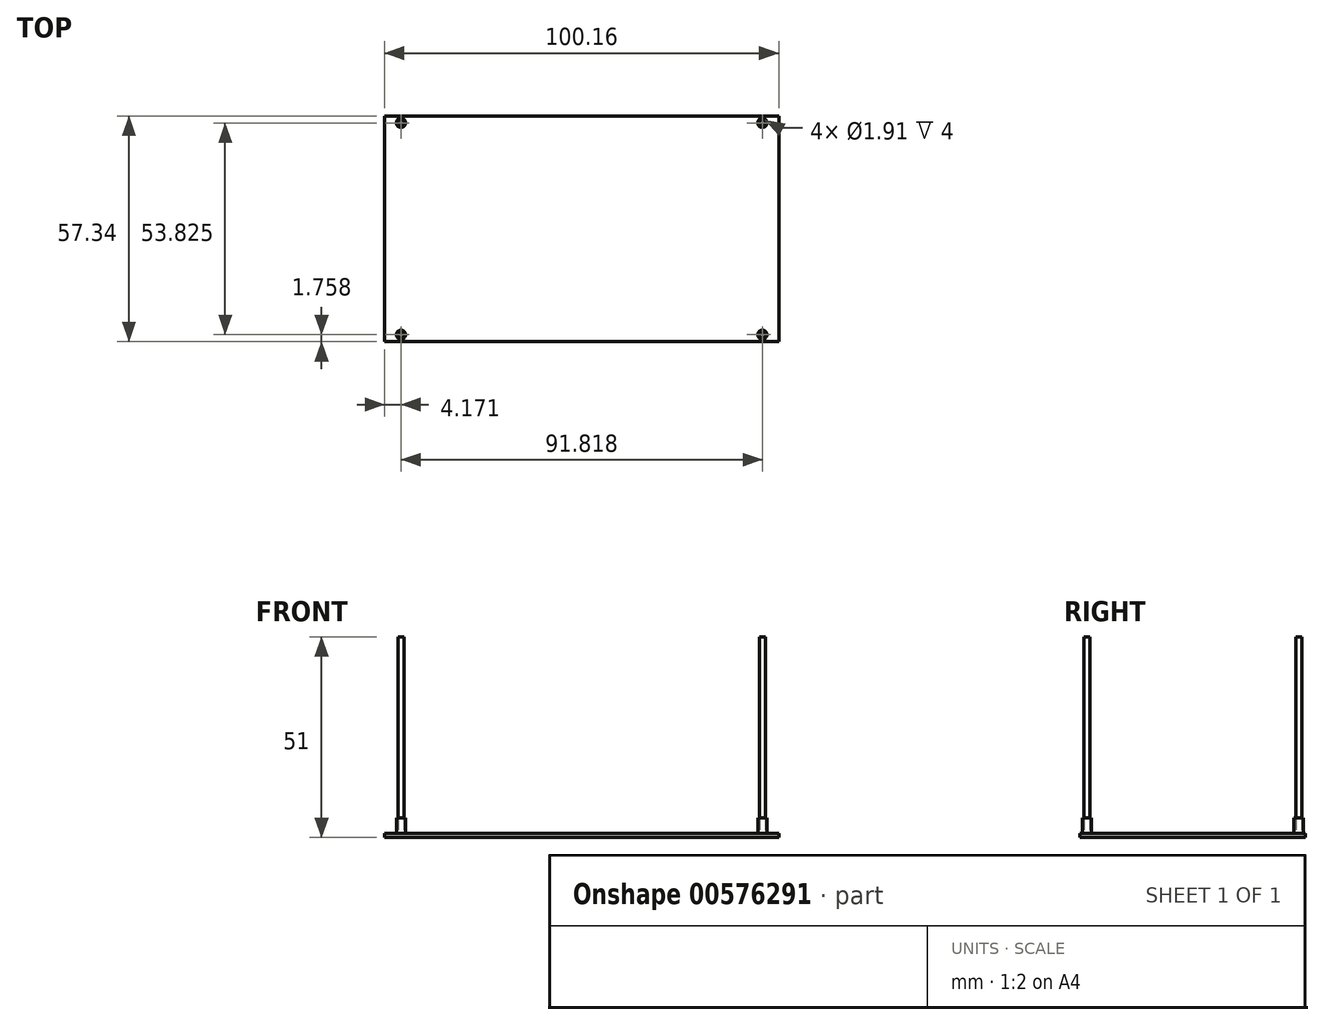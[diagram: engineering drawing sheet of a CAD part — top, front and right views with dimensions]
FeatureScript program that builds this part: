
annotation { "Feature Type Name" : "Feature", "Feature Type Description" : "" }
export const myFeature = defineFeature(function(context is Context, id is Id, definition is map)
    precondition{}
    {
        {
            var Q0;
            Q0=qCreatedBy(makeId("Top.planeOp"),FACE);
            var sketch = newSketch(context, id + "F0", { "sketchPlane" : qUnion([Q0])});
            skLineSegment(sketch, "E0.bottom", {"start": v(50.08, 28.67) * mm, "end": v(-50.08, 28.67) * mm});
            skLineSegment(sketch, "E0.top", {"start": v(50.08, -28.67) * mm, "end": v(-50.08, -28.67) * mm});
            skLineSegment(sketch, "E0.left", {"start": v(50.08, 28.67) * mm, "end": v(50.08, -28.67) * mm});
            skLineSegment(sketch, "E0.right", {"start": v(-50.08, 28.67) * mm, "end": v(-50.08, -28.67) * mm});
            skPoint(sketch, "E0.middle", {"position": v(0, 0) * mm});
            skSolve(sketch);
        }
        {
            var Q0;
            Q0 = qSketchRegion(id + "F0", true);
            extrude(context, id + "F1", {"entities" : qUnion([Q0]), "depth" : 1 * mm, "offsetDistance" : 25 * mm});
        }
        {
            var Q0;
            Q0=qCreatedBy(makeId("Top.planeOp"),FACE);
            var sketch = newSketch(context, id + "F2", { "sketchPlane" : qUnion([Q0])});
            skLineSegment(sketch, "E1", {"start": v(-50.08, 28.67) * mm, "end": v(-48.08, 28.67) * mm});
            skLineSegment(sketch, "E2", {"start": v(-48.08, 28.67) * mm, "end": v(-48.08, 26.67) * mm});
            skLineSegment(sketch, "E3", {"start": v(-48.08, 26.67) * mm, "end": v(-50.08, 26.67) * mm});
            skLineSegment(sketch, "E4", {"start": v(-50.08, 26.67) * mm, "end": v(-50.08, 28.67) * mm});
            skSolve(sketch);
        }
        {
            var Q0;
            Q0=makeQuery(id+"F1.opExtrude","CAP_FACE",FACE,{"disambiguationData":[OSD([sQuery(id+"F0.wireOp",EDGE,"E0.bottom"),sQuery(id+"F0.wireOp",EDGE,"E0.top"),sQuery(id+"F0.wireOp",EDGE,"E0.left"),sQuery(id+"F0.wireOp",EDGE,"E0.right")])],"isStart":false});
            var sketch = newSketch(context, id + "F3", { "sketchPlane" : qUnion([Q0])});
            skLineSegment(sketch, "E5", {"start": v(0, 0) * mm, "end": v(-64.87, 0) * mm, "construction": true});
            skPoint(sketch, "E5.endSnap0", {"position": v(-50.08, 0) * mm});
            skLineSegment(sketch, "E6", {"start": v(0, 0) * mm, "end": v(0, 40.05) * mm, "construction": true});
            skSolve(sketch);
        }
        {
            var Q0;
            Q0=makeQuery(id+"F3.imprint","IMPRINT",FACE,{"disambiguationData":[TD([[makeQuery(id+"F3.imprint","IMPRINT",EDGE,{"derivedFrom":makeQuery(id+"F1.opExtrude","CAP_EDGE",EDGE,{"disambiguationData":[OSD([sQuery(id+"F0.wireOp",EDGE,"E0.bottom")])],"isStart":false})}),1.0]])]});
            var sketch = newSketch(context, id + "F4", { "sketchPlane" : qUnion([Q0])});
            skCircle(sketch, "E7", {"center": v(-45.9, 26.92) * mm, "radius": 0.75 * mm});
            skSolve(sketch);
        }
        {
            var Q0;
            Q0 = qSketchRegion(id + "F4", true);
            var Q1;
            Q1=sQuery(id+"F4.wireOp",EDGE,"E7");
            extrude(context, id + "F5", {"entities" : qUnion([Q0]), "surfaceEntities" : qUnion([Q1]), "depth" : 50 * mm, "offsetDistance" : 25 * mm});
        }
        {
            var Q0;
            Q0=qCreatedBy(makeId("Top.planeOp"),FACE);
            var sketch = newSketch(context, id + "F6", { "sketchPlane" : qUnion([Q0])});
            skCircle(sketch, "E8", {"center": v(-45.9, 26.91) * mm, "radius": 0.95 * mm});
            skCircle(sketch, "E9", {"center": v(-45.9, 26.91) * mm, "radius": 1.16 * mm});
            skSolve(sketch);
        }
        {
            var Q0;
            Q0 = qSketchRegion(id + "F6", true);
            extrude(context, id + "F7", {"entities" : qUnion([Q0]), "depth" : 5 * mm, "offsetDistance" : 25 * mm});
        }
        {
            var Q0;
            Q0=makeQuery(id+"FUAeHRYxmnNsWtS_1.opExtrude","SWEPT_BODY",BODY,{"disambiguationData":[OSD([sQuery(id+"F2.wireOp",EDGE,"E1"),sQuery(id+"F2.wireOp",EDGE,"E2"),sQuery(id+"F2.wireOp",EDGE,"E3"),sQuery(id+"F2.wireOp",EDGE,"E4")])]});
            var Q1;
            Q1=makeQuery(id+"F5.opExtrude","SWEPT_BODY",BODY,{"disambiguationData":[OSD([sQuery(id+"F4.wireOp",EDGE,"E7")])]});
            var Q2;
            Q2=makeQuery(id+"F7.opExtrude","SWEPT_BODY",BODY,{"disambiguationData":[OSD([sQuery(id+"F6.wireOp",EDGE,"E8"),sQuery(id+"F6.wireOp",EDGE,"E9")])]});
            var Q3;
            Q3=qCreatedBy(makeId("Front.planeOp"),FACE);
            mirror(context, id + "F8", {"operationType" : NewBodyOperationType.ADD, "entities" : qUnion([Q0, Q1, Q2]), "mirrorPlane" : qUnion([Q3])});
        }
        {
            var Q0;
            Q0=makeQuery(id+"F1.opExtrude","SWEPT_BODY",BODY,{"disambiguationData":[OSD([sQuery(id+"F0.wireOp",EDGE,"E0.bottom"),sQuery(id+"F0.wireOp",EDGE,"E0.top"),sQuery(id+"F0.wireOp",EDGE,"E0.left"),sQuery(id+"F0.wireOp",EDGE,"E0.right")])]});
            var Q1;
            Q1=qCreatedBy(makeId("Right.planeOp"),FACE);
            mirror(context, id + "F9", {"operationType" : NewBodyOperationType.ADD, "entities" : qUnion([Q0]), "mirrorPlane" : qUnion([Q1])});
        }
    });
